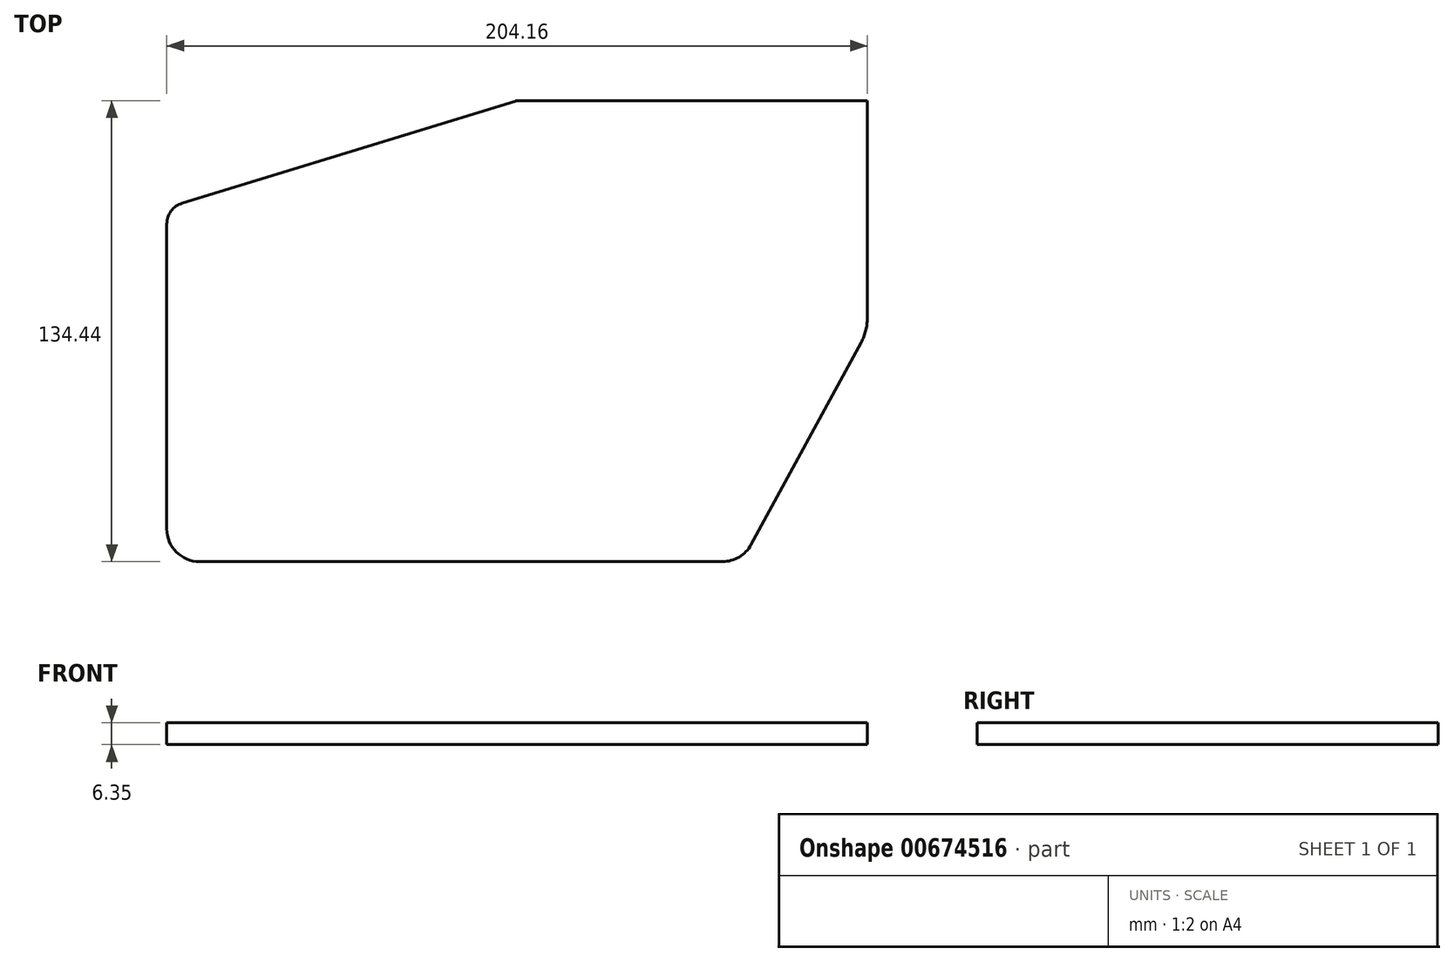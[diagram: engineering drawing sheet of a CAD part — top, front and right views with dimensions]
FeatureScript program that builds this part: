
annotation { "Feature Type Name" : "Feature", "Feature Type Description" : "" }
export const myFeature = defineFeature(function(context is Context, id is Id, definition is map)
    precondition{}
    {
        {
            var Q0;
            Q0=qCreatedBy(makeId("Top.planeOp"),FACE);
            var sketch = newSketch(context, id + "F0", { "sketchPlane" : qUnion([Q0])});
            skLineSegment(sketch, "E0.bottom", {"start": v(102.08, 67.22) * mm, "end": v(0.48, 67.22) * mm});
            skLineSegment(sketch, "E0.top", {"start": v(59.85, -67.22) * mm, "end": v(-92.55, -67.22) * mm});
            skLineSegment(sketch, "E0.left", {"start": v(102.08, 67.22) * mm, "end": v(102.08, 3.72) * mm});
            skLineSegment(sketch, "E0.right", {"start": v(-102.08, 31.2) * mm, "end": v(-102.08, -57.7) * mm});
            skPoint(sketch, "E0.middle", {"position": v(0, 0) * mm});
            skLineSegment(sketch, "E1", {"start": v(100.3, -3.26) * mm, "end": v(68.22, -62.24) * mm});
            skPoint(sketch, "E2.orphan", {"position": v(102.08, -67.22) * mm});
            skLineSegment(sketch, "E3", {"start": v(-97.59, 37.28) * mm, "end": v(-0.46, 67.08) * mm});
            skPoint(sketch, "E4.orphan", {"position": v(-102.08, 67.22) * mm});
            skPoint(sketch, "E5.visualSharp", {"position": v(-102.08, 35.9) * mm});
            skArc(sketch, "E5.filletArc", {"start": v(-97.59, 37.28) * mm, "mid": v(-100.83, 34.98) * mm, "end": v(-102.08, 31.2) * mm});
            skPoint(sketch, "E6.visualSharp", {"position": v(0, 67.22) * mm});
            skArc(sketch, "E6.filletArc", {"start": v(0.48, 67.22) * mm, "mid": v(0, 67.18) * mm, "end": v(-0.46, 67.08) * mm});
            skPoint(sketch, "E7.visualSharp", {"position": v(102.08, 0) * mm});
            skArc(sketch, "E7.filletArc", {"start": v(100.3, -3.26) * mm, "mid": v(101.63, 0.11) * mm, "end": v(102.08, 3.72) * mm});
            skPoint(sketch, "E8.visualSharp", {"position": v(65.51, -67.22) * mm});
            skArc(sketch, "E8.filletArc", {"start": v(59.85, -67.22) * mm, "mid": v(64.72, -65.88) * mm, "end": v(68.22, -62.24) * mm});
            skPoint(sketch, "E9.visualSharp", {"position": v(-102.08, -67.22) * mm});
            skArc(sketch, "E9.filletArc", {"start": v(-102.08, -57.7) * mm, "mid": v(-99.29, -64.43) * mm, "end": v(-92.55, -67.22) * mm});
            skSolve(sketch);
        }
        {
            var Q0;
            Q0 = qSketchRegion(id + "F0", true);
            extrude(context, id + "F1", {"entities" : qUnion([Q0]), "depth" : 6.35 * mm, "offsetDistance" : 25.4 * mm});
        }
    });
